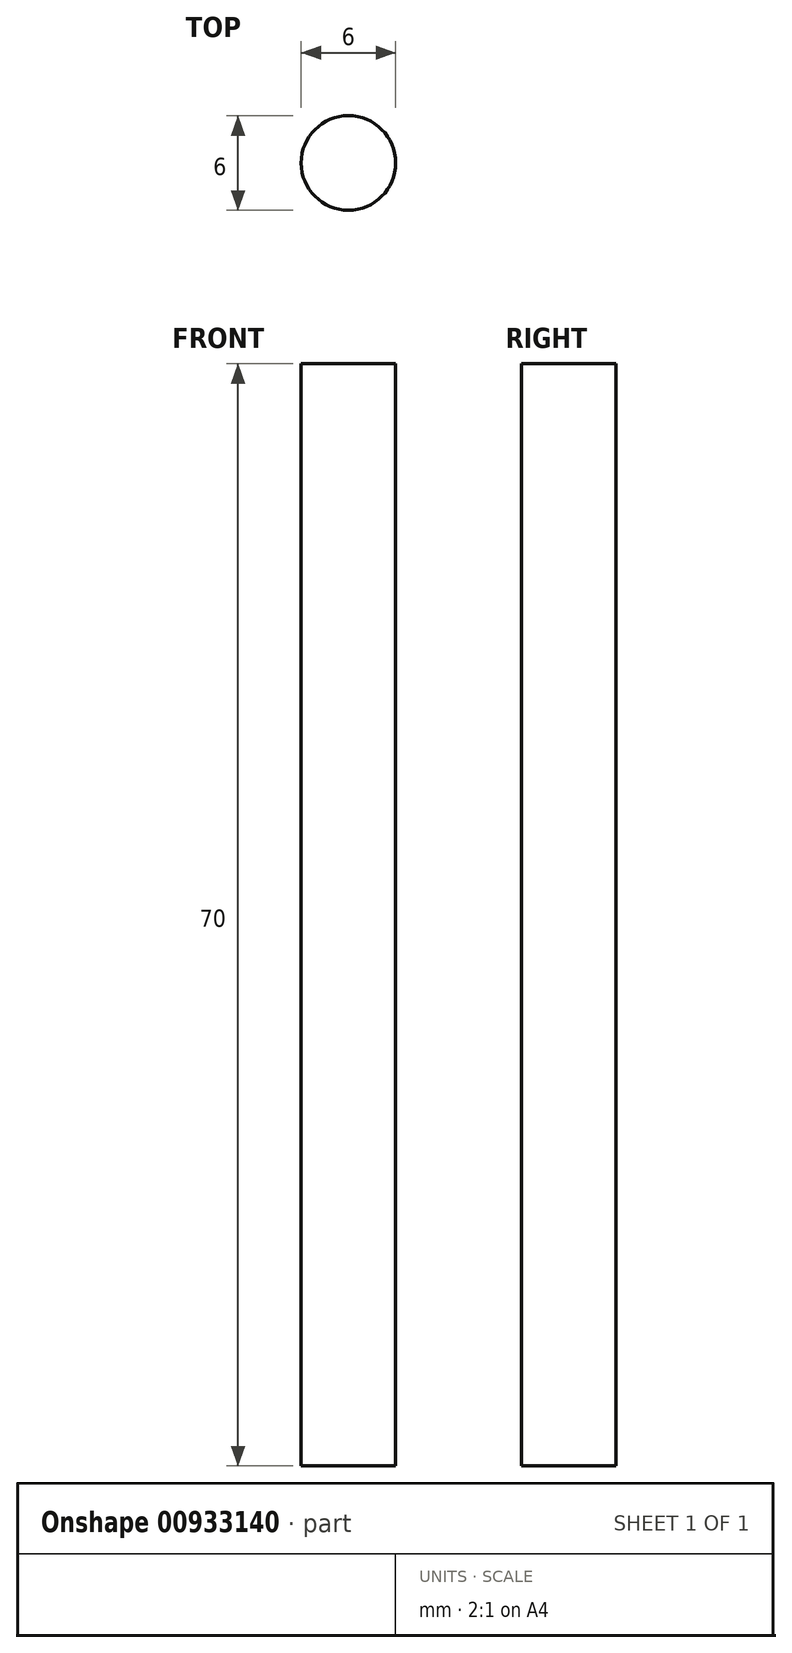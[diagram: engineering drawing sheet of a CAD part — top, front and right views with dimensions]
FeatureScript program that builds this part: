
annotation { "Feature Type Name" : "Feature", "Feature Type Description" : "" }
export const myFeature = defineFeature(function(context is Context, id is Id, definition is map)
    precondition{}
    {
        {
            var Q0;
            Q0=qCreatedBy(makeId("Top.planeOp"),FACE);
            var sketch = newSketch(context, id + "F0", { "sketchPlane" : qUnion([Q0])});
            skCircle(sketch, "E0", {"center": v(8, 11.13) * mm, "radius": 3 * mm});
            skSolve(sketch);
        }
        {
            var Q0;
            Q0=makeQuery(id+"F0.imprint","IMPRINT",FACE,{"disambiguationData":[TD([[makeQuery(id+"F0.imprint","IMPRINT",EDGE,{"derivedFrom":sQuery(id+"F0.wireOp",EDGE,"E0")}),1.0]])]});
            extrude(context, id + "F1", {"entities" : qUnion([Q0]), "depth" : 70 * mm, "offsetDistance" : 25 * mm});
        }
    });
